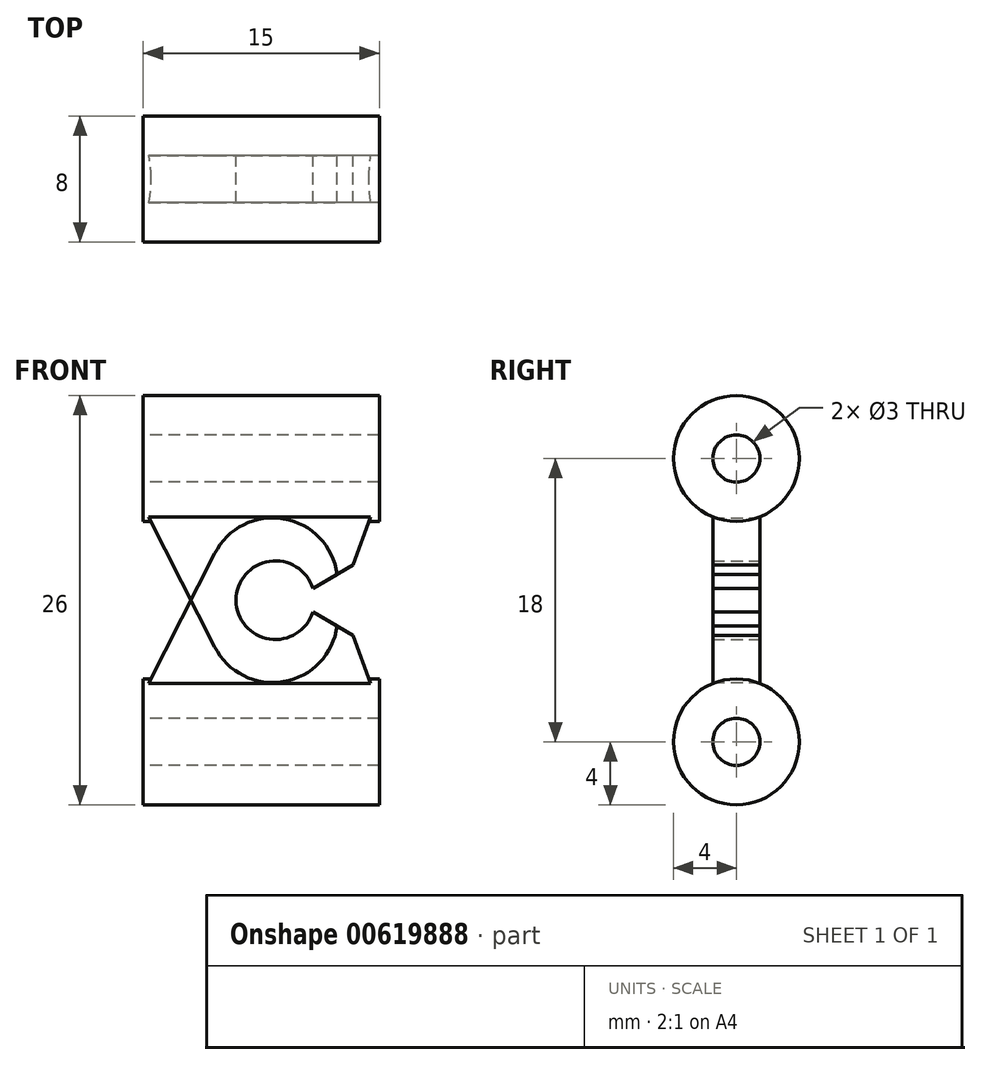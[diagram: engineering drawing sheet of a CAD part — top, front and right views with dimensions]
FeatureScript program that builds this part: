
annotation { "Feature Type Name" : "Feature", "Feature Type Description" : "" }
export const myFeature = defineFeature(function(context is Context, id is Id, definition is map)
    precondition{}
    {
        {
            var Q0;
            Q0=qCreatedBy(makeId("Right.planeOp"),FACE);
            var sketch = newSketch(context, id + "F0", { "sketchPlane" : qUnion([Q0])});
            skCircle(sketch, "E0", {"center": v(0, 0) * mm, "radius": 1.5 * mm});
            skCircle(sketch, "E1", {"center": v(0, 0) * mm, "radius": 4 * mm});
            skSolve(sketch);
        }
        {
            var Q0;
            Q0=makeQuery(id+"F0.imprint","IMPRINT",FACE,{"disambiguationData":[TD([[makeQuery(id+"F0.imprint","IMPRINT",EDGE,{"derivedFrom":sQuery(id+"F0.wireOp",EDGE,"E0")}),-1.0]])]});
            var Q1;
            Q1=qConstructionFilter(qBodyType(qCreatedBy(id+"F0",EDGE),BodyType.WIRE),ConstructionObject.NO);
            extrude(context, id + "F1", {"entities" : qUnion([Q0]), "surfaceEntities" : qUnion([Q1]), "depth" : 15 * mm, "offsetDistance" : 25 * mm});
        }
        {
            var Q0;
            Q0=qCreatedBy(makeId("Front.planeOp"),FACE);
            var sketch = newSketch(context, id + "F2", { "sketchPlane" : qUnion([Q0])});
            skLineSegment(sketch, "E2", {"start": v(0, -3) * mm, "end": v(14.7, -3) * mm});
            skArc(sketch, "E3", {"start": v(10.79, -8.25) * mm, "mid": v(5.9, -9) * mm, "end": v(10.79, -9.75) * mm});
            skLineSegment(sketch, "E4", {"start": v(0, -3) * mm, "end": v(4.55, -11.97) * mm});
            skArc(sketch, "E5", {"start": v(4.55, -11.97) * mm, "mid": v(8.93, -14.17) * mm, "end": v(12.32, -10.64) * mm});
            skLineSegment(sketch, "E6", {"start": v(14.7, -3) * mm, "end": v(13.34, -6.78) * mm});
            skLineSegment(sketch, "E7", {"start": v(12.32, -10.64) * mm, "end": v(10.79, -9.75) * mm});
            skLineSegment(sketch, "E8", {"start": v(13.34, -6.78) * mm, "end": v(10.79, -8.25) * mm});
            skLineSegment(sketch, "E9", {"start": v(8.4, -9) * mm, "end": v(24, -9) * mm, "construction": true});
            skLineSegment(sketch, "E10", {"start": v(10.79, -9.75) * mm, "end": v(9.49, -9) * mm, "construction": true});
            skLineSegment(sketch, "E11", {"start": v(9.49, -9) * mm, "end": v(10.79, -8.25) * mm, "construction": true});
            skSolve(sketch);
        }
        {
            var Q0;
            Q0=makeQuery(id+"F2.imprint","IMPRINT",FACE,{"disambiguationData":[TD([[makeQuery(id+"F2.imprint","IMPRINT",EDGE,{"derivedFrom":sQuery(id+"F2.wireOp",EDGE,"E2")}),-1.0]])]});
            extrude(context, id + "F3", {"entities" : qUnion([Q0]), "operationType" : NewBodyOperationType.ADD, "endBound" : BoundingType.SYMMETRIC, "depth" : 3 * mm, "offsetDistance" : 25 * mm});
        }
        {
            var Q0;
            Q0=qCreatedBy(makeId("Top.planeOp"),FACE);
            cPlane(context, id + "F4", {"entities" : qUnion([Q0]), "cplaneType" : CPlaneType.OFFSET, "offset" : 9 * mm, "oppositeDirection" : true, "width" : 150 * mm, "height" : 150 * mm});
        }
        {
            var Q0;
            Q0=makeQuery(id+"F1.opExtrude","SWEPT_BODY",BODY,{"disambiguationData":[OSD([sQuery(id+"F0.wireOp",EDGE,"E0"),sQuery(id+"F0.wireOp",EDGE,"E1")])]});
            var Q1;
            Q1=qCreatedBy(id+"F4.planeOp",FACE);
            mirror(context, id + "F5", {"entities" : qUnion([Q0]), "mirrorPlane" : qUnion([Q1])});
        }
    });
